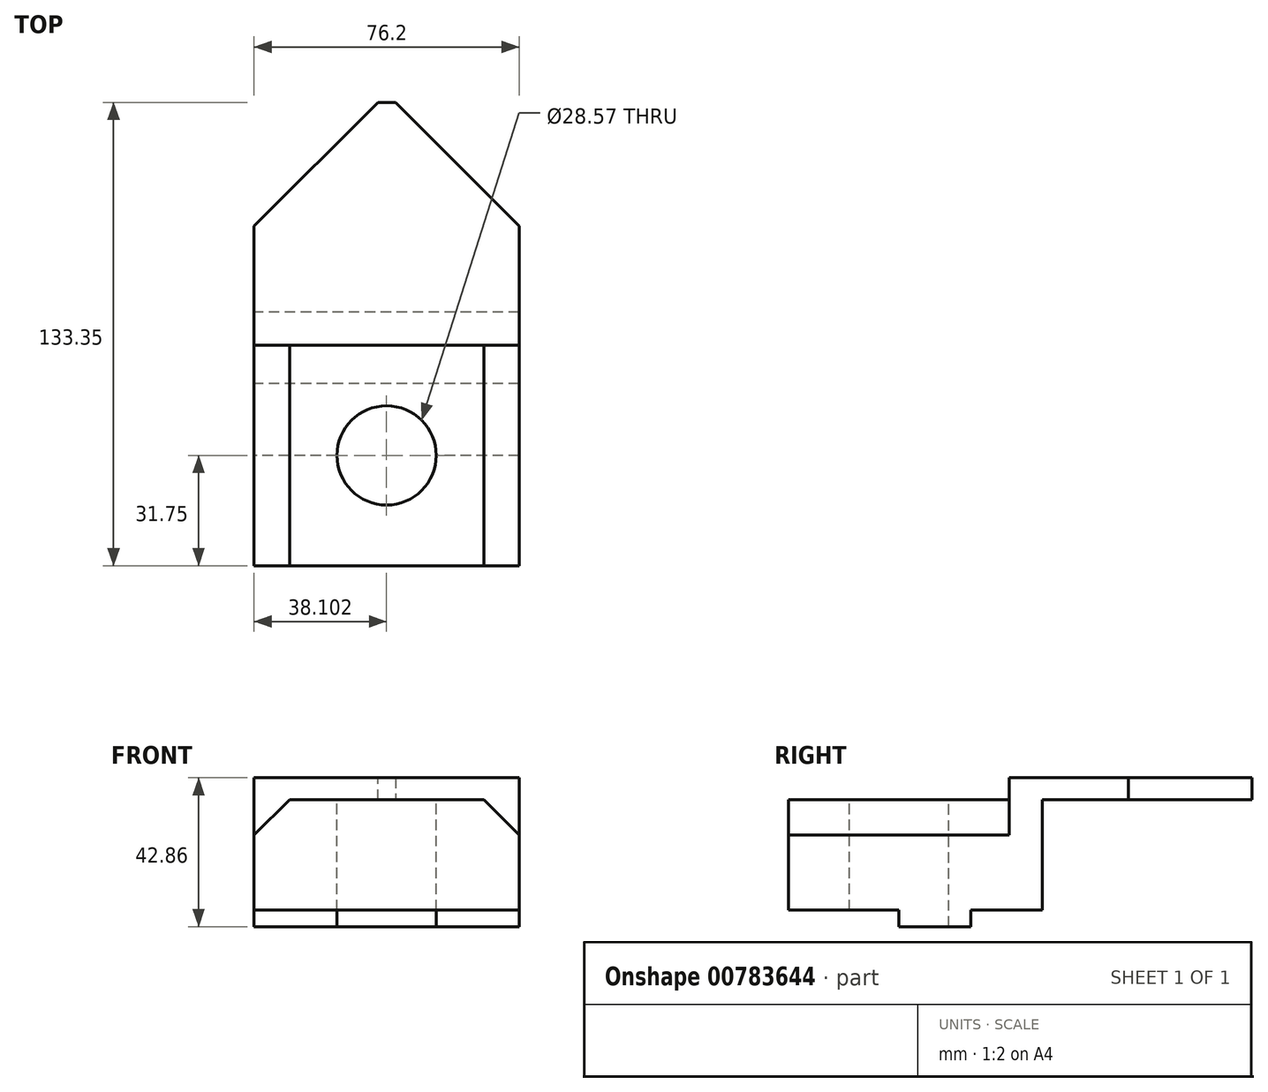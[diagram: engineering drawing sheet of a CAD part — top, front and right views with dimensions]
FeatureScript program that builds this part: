
annotation { "Feature Type Name" : "Feature", "Feature Type Description" : "" }
export const myFeature = defineFeature(function(context is Context, id is Id, definition is map)
    precondition{}
    {
        {
            var Q0;
            Q0=qCreatedBy(makeId("Front.planeOp"),FACE);
            var sketch = newSketch(context, id + "F0", { "sketchPlane" : qUnion([Q0])});
            skLineSegment(sketch, "E0", {"start": v(-57.05, -21.74) * mm, "end": v(19.15, -21.74) * mm});
            skLineSegment(sketch, "E1", {"start": v(19.15, -21.74) * mm, "end": v(19.15, -26.5) * mm});
            skLineSegment(sketch, "E2", {"start": v(19.15, -26.5) * mm, "end": v(-57.05, -26.5) * mm});
            skLineSegment(sketch, "E3", {"start": v(-57.05, -26.5) * mm, "end": v(-57.05, -21.74) * mm});
            skLineSegment(sketch, "E4", {"start": v(19.15, -21.74) * mm, "end": v(19.15, 10.01) * mm});
            skLineSegment(sketch, "E5", {"start": v(19.15, 10.01) * mm, "end": v(-57.05, 10.01) * mm});
            skLineSegment(sketch, "E6", {"start": v(-57.05, 10.01) * mm, "end": v(-57.05, -21.74) * mm});
            skLineSegment(sketch, "E7", {"start": v(-57.05, 10.01) * mm, "end": v(-57.05, 16.36) * mm});
            skLineSegment(sketch, "E8", {"start": v(-57.05, 16.36) * mm, "end": v(19.15, 16.36) * mm});
            skLineSegment(sketch, "E9", {"start": v(19.15, 16.36) * mm, "end": v(19.15, 10.01) * mm});
            skSolve(sketch);
        }
        {
            var Q0;
            Q0=makeQuery(id+"F0.imprint","IMPRINT",FACE,{"disambiguationData":[TD([[makeQuery(id+"F0.imprint","IMPRINT",EDGE,{"derivedFrom":sQuery(id+"F0.wireOp",EDGE,"E0")}),1.0]])]});
            var Q1;
            Q1=makeQuery(id+"F0.imprint","IMPRINT",FACE,{"disambiguationData":[TD([[makeQuery(id+"F0.imprint","IMPRINT",EDGE,{"derivedFrom":sQuery(id+"F0.wireOp",EDGE,"E0")}),-1.0]])]});
            extrude(context, id + "F1", {"entities" : qUnion([Q0, Q1]), "depth" : 133.35 * mm, "offsetDistance" : 25.4 * mm});
        }
        {
            var Q0;
            Q0=makeQuery(id+"F1.opExtrude","SWEPT_EDGE",EDGE,{"disambiguationData":[OSD([sQuery(id+"F0.wireOp",EDGE,"E4"),sQuery(id+"F0.wireOp",EDGE,"E5"),sQuery(id+"F0.wireOp",EDGE,"E9")])]});
            var Q1;
            Q1=makeQuery(id+"F1.opExtrude","SWEPT_EDGE",EDGE,{"disambiguationData":[OSD([sQuery(id+"F0.wireOp",EDGE,"E5"),sQuery(id+"F0.wireOp",EDGE,"E6"),sQuery(id+"F0.wireOp",EDGE,"E7")])]});
            chamfer(context, id + "F2", {"entities" : qUnion([Q0, Q1]), "width" : 10.16 * mm, "tangentPropagation" : true});
        }
        {
            var Q0;
            Q0=makeQuery(id+"F0.imprint","IMPRINT",FACE,{"disambiguationData":[TD([[makeQuery(id+"F0.imprint","IMPRINT",EDGE,{"derivedFrom":sQuery(id+"F0.wireOp",EDGE,"E0")}),1.0]])]});
            var Q1;
            Q1=makeQuery(id+"F0.imprint","IMPRINT",FACE,{"disambiguationData":[TD([[makeQuery(id+"F0.imprint","IMPRINT",EDGE,{"derivedFrom":sQuery(id+"F0.wireOp",EDGE,"E5")}),-1.0]])]});
            extrude(context, id + "F3", {"entities" : qUnion([Q0, Q1]), "operationType" : NewBodyOperationType.ADD, "oppositeDirection" : true, "depth" : 9.52 * mm, "offsetDistance" : 25.4 * mm});
        }
        {
            var Q0;
            Q0=makeQuery(id+"F0.imprint","IMPRINT",FACE,{"disambiguationData":[TD([[makeQuery(id+"F0.imprint","IMPRINT",EDGE,{"derivedFrom":sQuery(id+"F0.wireOp",EDGE,"E5")}),-1.0]])]});
            extrude(context, id + "F4", {"entities" : qUnion([Q0]), "operationType" : NewBodyOperationType.ADD, "oppositeDirection" : true, "depth" : 69.85 * mm, "offsetDistance" : 25.4 * mm});
        }
        {
            var Q0;
            Q0=makeQuery(id+"F1.opExtrude","SWEPT_FACE",FACE,{"disambiguationData":[OSD([sQuery(id+"F0.wireOp",EDGE,"E5")])]});
            var sketch = newSketch(context, id + "F5", { "sketchPlane" : qUnion([Q0])});
            skLineSegment(sketch, "E10", {"start": v(-46.89, -63.5) * mm, "end": v(9, -63.5) * mm});
            skLineSegment(sketch, "E11", {"start": v(-46.89, -63.5) * mm, "end": v(-73.67, -63.5) * mm});
            skLineSegment(sketch, "E12", {"start": v(-73.67, -63.5) * mm, "end": v(-73.67, -133.35) * mm});
            skLineSegment(sketch, "E13", {"start": v(-73.67, -133.35) * mm, "end": v(35.78, -133.35) * mm});
            skLineSegment(sketch, "E14", {"start": v(35.78, -133.35) * mm, "end": v(35.78, -63.5) * mm});
            skLineSegment(sketch, "E15", {"start": v(35.78, -63.5) * mm, "end": v(9, -63.5) * mm});
            skSolve(sketch);
        }
        {
            var Q0;
            Q0 = qSketchRegion(id + "F5", true);
            extrude(context, id + "F6", {"entities" : qUnion([Q0]), "operationType" : NewBodyOperationType.REMOVE, "oppositeDirection" : true, "depth" : 51.3 * mm, "offsetDistance" : 25.4 * mm});
        }
        {
            var Q0;
            Q0=makeQuery(id+"F4.opExtrude","CAP_EDGE",EDGE,{"disambiguationData":[OSD([sQuery(id+"F0.wireOp",EDGE,"E7")])],"isStart":false});
            var Q1;
            Q1=makeQuery(id+"F4.opExtrude","CAP_EDGE",EDGE,{"disambiguationData":[OSD([sQuery(id+"F0.wireOp",EDGE,"E9")])],"isStart":false});
            chamfer(context, id + "F7", {"entities" : qUnion([Q0, Q1]), "chamferType" : ChamferType.OFFSET_ANGLE, "width" : 35.56 * mm, "oppositeDirection" : false, "angle" : 45 * degree, "tangentPropagation" : true});
        }
        {
            var Q0;
            Q0=makeQuery(id+"F1.opExtrude","SWEPT_FACE",FACE,{"disambiguationData":[OSD([sQuery(id+"F0.wireOp",EDGE,"E5")])]});
            var sketch = newSketch(context, id + "F8", { "sketchPlane" : qUnion([Q0])});
            skPoint(sketch, "E16.endSnap0", {"position": v(-46.89, -31.75) * mm});
            skCircle(sketch, "E17", {"center": v(-18.95, -31.75) * mm, "radius": 14.29 * mm});
            skSolve(sketch);
        }
        {
            var Q0;
            Q0 = qSketchRegion(id + "F8", true);
            extrude(context, id + "F9", {"entities" : qUnion([Q0]), "operationType" : NewBodyOperationType.REMOVE, "oppositeDirection" : true, "depth" : 39.12 * mm, "offsetDistance" : 25.4 * mm});
        }
        {
            var Q0;
            Q0=makeQuery(id+"F1.opExtrude","CAP_FACE",FACE,{"disambiguationData":[OSD([sQuery(id+"F0.wireOp",EDGE,"E1"),sQuery(id+"F0.wireOp",EDGE,"E2"),sQuery(id+"F0.wireOp",EDGE,"E3"),sQuery(id+"F0.wireOp",EDGE,"E4"),sQuery(id+"F0.wireOp",EDGE,"E5"),sQuery(id+"F0.wireOp",EDGE,"E6")])],"isStart":true});
            extrude(context, id + "F10", {"entities" : qUnion([Q0]), "operationType" : NewBodyOperationType.ADD, "depth" : 9.52 * mm, "offsetDistance" : 25.4 * mm});
        }
        {
            var Q0;
            {var subQ0=sQuery(id+"F0.wireOp",EDGE,"E6");var subQ1=sQuery(id+"F0.wireOp",EDGE,"E3");var subQ2=sQuery(id+"F0.wireOp",EDGE,"E7");Q0=makeQuery(id+"F10.boolean.opBoolean","MERGE",FACE,{"derivedFrom":[makeQuery(id+"F4.boolean.opBoolean","MERGE",FACE,{"derivedFrom":[makeQuery(id+"F3.boolean.opBoolean","MERGE",FACE,{"derivedFrom":[makeQuery(id+"F1.opExtrude","SWEPT_FACE",FACE,{"disambiguationData":[OSD([subQ1,subQ0])]}),makeQuery(id+"F3.opExtrude","SWEPT_FACE",FACE,{"disambiguationData":[OSD([subQ0,subQ2])]})]}),makeQuery(id+"F4.opExtrude","SWEPT_FACE",FACE,{"disambiguationData":[OSD([subQ2])]})]}),makeQuery(id+"F10.opExtrude","SWEPT_FACE",FACE,{"disambiguationData":[OSD([subQ1,subQ0])]})]});}
            var sketch = newSketch(context, id + "F11", { "sketchPlane" : qUnion([Q0])});
            skLineSegment(sketch, "E18", {"start": v(31.75, -26.5) * mm, "end": v(31.75, -21.74) * mm});
            skLineSegment(sketch, "E19", {"start": v(31.75, -21.74) * mm, "end": v(63.5, -21.74) * mm});
            skLineSegment(sketch, "E20", {"start": v(31.75, -26.5) * mm, "end": v(11.11, -26.5) * mm});
            skLineSegment(sketch, "E21", {"start": v(11.11, -26.5) * mm, "end": v(11.11, -21.74) * mm});
            skLineSegment(sketch, "E22", {"start": v(11.11, -21.74) * mm, "end": v(-9.52, -21.74) * mm});
            skSolve(sketch);
        }
        {
            var Q0;
            Q0 = qSketchRegion(id + "F11", true);
            var Q1;
            {var subQ0=sQuery(id+"F11.wireOp",EDGE,"E21");Q1=makeQuery(id+"F11.imprint","IMPRINT",FACE,{"disambiguationData":[TD([[makeQuery(id+"F11.imprint","IMPRINT",EDGE,{"derivedFrom":subQ0}),1.0]])]});}
            var Q2;
            {var subQ0=sQuery(id+"F11.wireOp",EDGE,"E18");Q2=makeQuery(id+"F11.imprint","IMPRINT",FACE,{"disambiguationData":[TD([[makeQuery(id+"F11.imprint","IMPRINT",EDGE,{"derivedFrom":subQ0}),-1.0]])]});}
            extrude(context, id + "F12", {"entities" : qUnion([Q0, Q1, Q2]), "operationType" : NewBodyOperationType.REMOVE, "oppositeDirection" : true, "depth" : 84.84 * mm, "offsetDistance" : 25.4 * mm});
        }
    });
